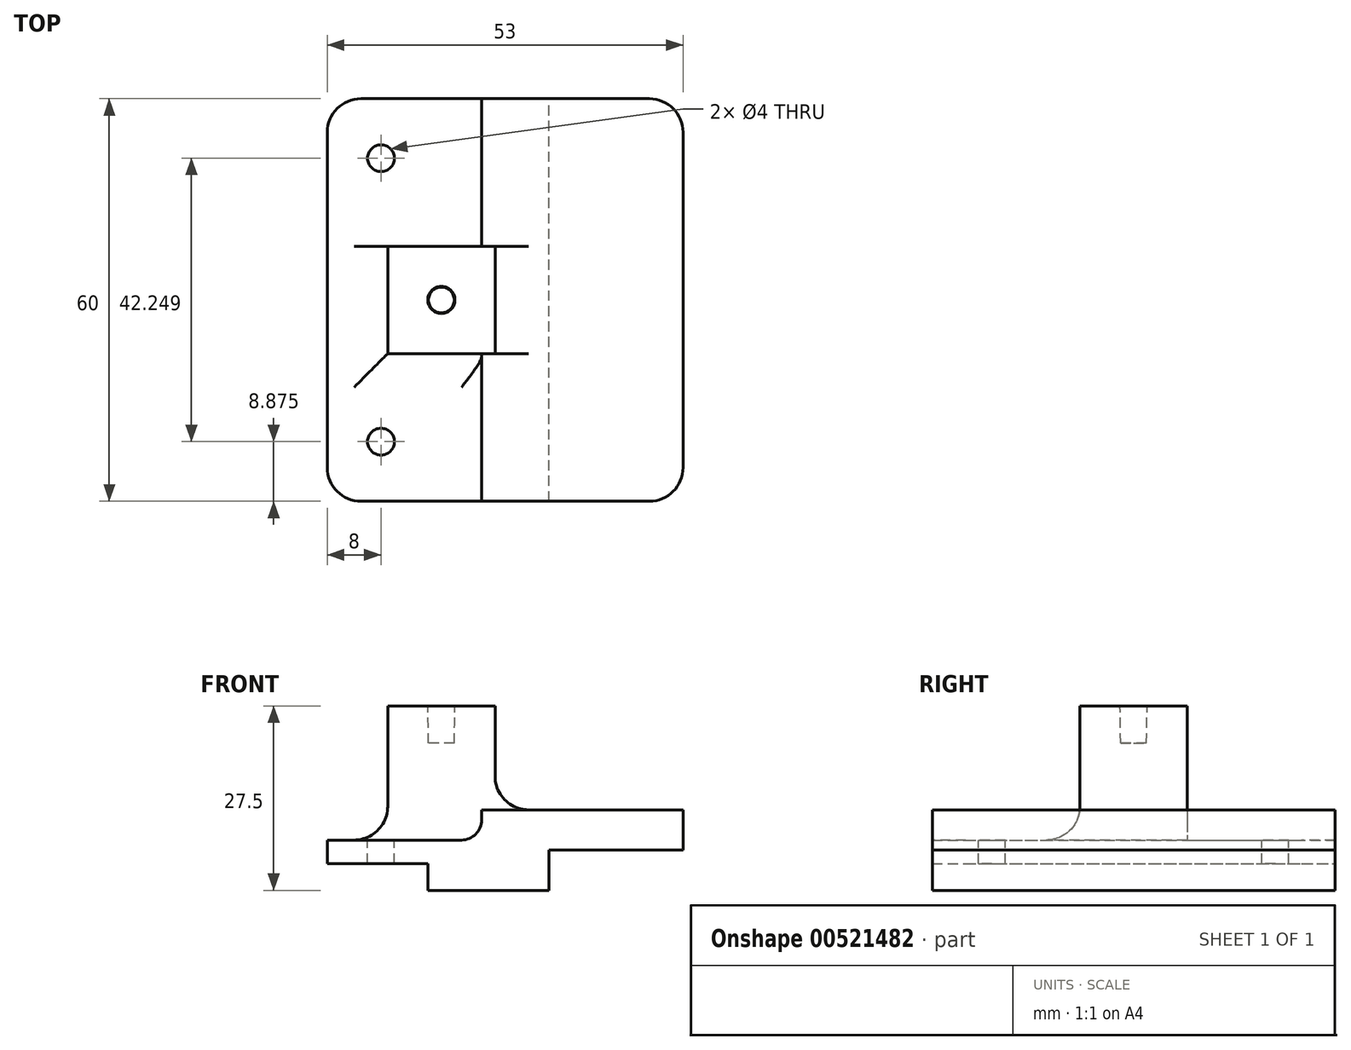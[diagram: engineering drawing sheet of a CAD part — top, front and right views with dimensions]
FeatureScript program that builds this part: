
annotation { "Feature Type Name" : "Feature", "Feature Type Description" : "" }
export const myFeature = defineFeature(function(context is Context, id is Id, definition is map)
    precondition{}
    {
        {
            var Q0;
            Q0=qCreatedBy(makeId("Front.planeOp"),FACE);
            var sketch = newSketch(context, id + "F0", { "sketchPlane" : qUnion([Q0])});
            skLineSegment(sketch, "E0", {"start": v(-15, 0) * mm, "end": v(-15, 3.5) * mm});
            skLineSegment(sketch, "E1", {"start": v(-15, 3.5) * mm, "end": v(8, 3.5) * mm});
            skLineSegment(sketch, "E2", {"start": v(8, 3.5) * mm, "end": v(8, 8) * mm});
            skLineSegment(sketch, "E3", {"start": v(8, 8) * mm, "end": v(38, 8) * mm});
            skLineSegment(sketch, "E4", {"start": v(38, 8) * mm, "end": v(38, 2) * mm});
            skLineSegment(sketch, "E5", {"start": v(38, 2) * mm, "end": v(18, 2) * mm});
            skLineSegment(sketch, "E6", {"start": v(18, 2) * mm, "end": v(18, -4) * mm});
            skLineSegment(sketch, "E7", {"start": v(18, -4) * mm, "end": v(0, -4) * mm});
            skLineSegment(sketch, "E8", {"start": v(0, -4) * mm, "end": v(0, 0) * mm});
            skLineSegment(sketch, "E9", {"start": v(0, 0) * mm, "end": v(-15, 0) * mm});
            skSolve(sketch);
        }
        {
            var Q0;
            Q0=makeQuery(id+"F0.imprint","IMPRINT",FACE,{"disambiguationData":[TD([[makeQuery(id+"F0.imprint","IMPRINT",EDGE,{"derivedFrom":sQuery(id+"F0.wireOp",EDGE,"E0")}),-1.0]])]});
            extrude(context, id + "F1", {"entities" : qUnion([Q0]), "endBound" : BoundingType.SYMMETRIC, "depth" : 60 * mm, "offsetDistance" : 25 * mm});
        }
        {
            var Q0;
            Q0=makeQuery(id+"F1.opExtrude","SWEPT_FACE",FACE,{"disambiguationData":[OSD([sQuery(id+"F0.wireOp",EDGE,"E1")])]});
            var sketch = newSketch(context, id + "F2", { "sketchPlane" : qUnion([Q0])});
            skLineSegment(sketch, "E10", {"start": v(-7, 21.12) * mm, "end": v(-7, -21.12) * mm, "construction": true});
            skCircle(sketch, "E11", {"center": v(-7, 21.12) * mm, "radius": 2 * mm});
            skCircle(sketch, "E12", {"center": v(-7, -21.12) * mm, "radius": 2 * mm});
            skPoint(sketch, "E13", {"position": v(-7, 0) * mm});
            skLineSegment(sketch, "E14.bottom", {"start": v(-15, 8) * mm, "end": v(1, 8) * mm});
            skLineSegment(sketch, "E14.top", {"start": v(-15, -8) * mm, "end": v(1, -8) * mm});
            skLineSegment(sketch, "E14.left", {"start": v(-15, 8) * mm, "end": v(-15, -8) * mm});
            skLineSegment(sketch, "E14.right", {"start": v(1, 8) * mm, "end": v(1, -8) * mm});
            skSolve(sketch);
        }
        {
            var Q0;
            Q0=makeQuery(id+"F2.imprint","IMPRINT",FACE,{"disambiguationData":[TD([[makeQuery(id+"F2.imprint","IMPRINT",EDGE,{"derivedFrom":sQuery(id+"F2.wireOp",EDGE,"E14.bottom")}),-1.0]])]});
            extrude(context, id + "F3", {"entities" : qUnion([Q0]), "operationType" : NewBodyOperationType.ADD, "depth" : 20 * mm, "offsetDistance" : 25 * mm});
        }
        {
            var Q0;
            Q0=makeQuery(id+"F2.imprint","IMPRINT",FACE,{"disambiguationData":[TD([[makeQuery(id+"F2.imprint","IMPRINT",EDGE,{"derivedFrom":sQuery(id+"F2.wireOp",EDGE,"E11")}),1.0]])]});
            var Q1;
            Q1=makeQuery(id+"F2.imprint","IMPRINT",FACE,{"disambiguationData":[TD([[makeQuery(id+"F2.imprint","IMPRINT",EDGE,{"derivedFrom":sQuery(id+"F2.wireOp",EDGE,"E12")}),1.0]])]});
            extrude(context, id + "F4", {"entities" : qUnion([Q0, Q1]), "operationType" : NewBodyOperationType.REMOVE, "oppositeDirection" : true, "depth" : 25 * mm, "offsetDistance" : 25 * mm});
        }
        {
            var Q0;
            Q0=makeQuery(id+"F3.opExtrude","SWEPT_FACE",FACE,{"disambiguationData":[OSD([sQuery(id+"F2.wireOp",EDGE,"E14.right")])]});
            extrude(context, id + "F5", {"entities" : qUnion([Q0]), "operationType" : NewBodyOperationType.ADD, "depth" : 9 * mm, "offsetDistance" : 25 * mm});
        }
        {
            var Q0;
            Q0=makeQuery(id+"F3.boolean.opBoolean","MERGE",FACE,{"derivedFrom":[makeQuery(id+"F1.opExtrude","SWEPT_FACE",FACE,{"disambiguationData":[OSD([sQuery(id+"F0.wireOp",EDGE,"E0")])]}),makeQuery(id+"F3.opExtrude","SWEPT_FACE",FACE,{"disambiguationData":[OSD([sQuery(id+"F2.wireOp",EDGE,"E14.left")])]})]});
            var sketch = newSketch(context, id + "F6", { "sketchPlane" : qUnion([Q0])});
            skLineSegment(sketch, "E15.bottom", {"start": v(-8, 23.5) * mm, "end": v(8, 23.5) * mm});
            skLineSegment(sketch, "E15.top", {"start": v(-8, 3.5) * mm, "end": v(8, 3.5) * mm});
            skLineSegment(sketch, "E15.left", {"start": v(-8, 23.5) * mm, "end": v(-8, 3.5) * mm});
            skLineSegment(sketch, "E15.right", {"start": v(8, 23.5) * mm, "end": v(8, 3.5) * mm});
            skSolve(sketch);
        }
        {
            var Q0;
            Q0=makeQuery(id+"F6.imprint","IMPRINT",FACE,{"disambiguationData":[TD([[makeQuery(id+"F6.imprint","IMPRINT",EDGE,{"derivedFrom":sQuery(id+"F6.wireOp",EDGE,"E15.bottom")}),1.0]])]});
            extrude(context, id + "F7", {"entities" : qUnion([Q0]), "operationType" : NewBodyOperationType.REMOVE, "oppositeDirection" : true, "depth" : 9 * mm, "offsetDistance" : 25 * mm});
        }
        {
            var Q0;
            Q0=makeQuery(id+"F1.opExtrude","SWEPT_EDGE",EDGE,{"disambiguationData":[OSD([sQuery(id+"F0.wireOp",EDGE,"E1"),sQuery(id+"F0.wireOp",EDGE,"E2")])]});
            fillet(context, id + "F8", {"entities" : qUnion([Q0]), "radius" : 3 * mm, "tangentPropagation" : true, "allowEdgeOverflow" : false});
        }
        {
            var Q0;
            Q0=makeQuery(id+"F1.opExtrude","CAP_EDGE",EDGE,{"disambiguationData":[OSD([sQuery(id+"F0.wireOp",EDGE,"E0")])],"isStart":false});
            var Q1;
            Q1=makeQuery(id+"F1.opExtrude","CAP_EDGE",EDGE,{"disambiguationData":[OSD([sQuery(id+"F0.wireOp",EDGE,"E0")])],"isStart":true});
            var Q2;
            Q2=makeQuery(id+"F1.opExtrude","CAP_EDGE",EDGE,{"disambiguationData":[OSD([sQuery(id+"F0.wireOp",EDGE,"E4")])],"isStart":false});
            var Q3;
            Q3=makeQuery(id+"F1.opExtrude","CAP_EDGE",EDGE,{"disambiguationData":[OSD([sQuery(id+"F0.wireOp",EDGE,"E4")])],"isStart":true});
            fillet(context, id + "F9", {"entities" : qUnion([Q0, Q1, Q2, Q3]), "radius" : 5 * mm, "tangentPropagation" : true, "allowEdgeOverflow" : false});
        }
        {
            var Q0;
            Q0=makeQuery(id+"F7.boolean.opBoolean","COPY",EDGE,{"derivedFrom":makeQuery(id+"F7.opExtrude","CAP_EDGE",EDGE,{"disambiguationData":[OSD([sQuery(id+"F6.wireOp",EDGE,"E15.top")])],"isStart":false})});
            var Q1;
            {var subQ0=sQuery(id+"F2.wireOp",EDGE,"E14.right");var subQ1=sQuery(id+"F2.wireOp",EDGE,"E14.top");Q1=makeQuery(id+"F5.boolean.opBoolean","MERGE",EDGE,{"derivedFrom":[makeQuery(id+"F3.opExtrude","CAP_EDGE",EDGE,{"disambiguationData":[OSD([subQ1])],"isStart":true}),makeQuery(id+"F5.opExtrude","SWEPT_EDGE",EDGE,{"disambiguationData":[OSD([subQ1,subQ0]),TDD([makeQuery(id+"F3.opExtrude","CAP_VERTEX",VERTEX,{"disambiguationData":[OSD([subQ1,subQ0])],"isStart":true})])]})]});}
            var Q2;
            {var subQ0=sQuery(id+"F2.wireOp",EDGE,"E14.right");var subQ1=sQuery(id+"F2.wireOp",EDGE,"E14.bottom");Q2=makeQuery(id+"F5.boolean.opBoolean","MERGE",EDGE,{"derivedFrom":[makeQuery(id+"F3.opExtrude","CAP_EDGE",EDGE,{"disambiguationData":[OSD([subQ1])],"isStart":true}),makeQuery(id+"F5.opExtrude","SWEPT_EDGE",EDGE,{"disambiguationData":[OSD([subQ1,subQ0]),TDD([makeQuery(id+"F3.opExtrude","CAP_VERTEX",VERTEX,{"disambiguationData":[OSD([subQ1,subQ0])],"isStart":true})])]})]});}
            fillet(context, id + "F10", {"entities" : qUnion([Q0, Q1, Q2]), "radius" : 5 * mm, "tangentPropagation" : true, "allowEdgeOverflow" : false});
        }
        {
            var Q0;
            Q0=makeQuery(id+"F3.opExtrude","CAP_FACE",FACE,{"disambiguationData":[OSD([sQuery(id+"F2.wireOp",EDGE,"E14.bottom"),sQuery(id+"F2.wireOp",EDGE,"E14.top"),sQuery(id+"F2.wireOp",EDGE,"E14.left"),sQuery(id+"F2.wireOp",EDGE,"E14.right")])],"isStart":false});
            var sketch = newSketch(context, id + "F11", { "sketchPlane" : qUnion([Q0])});
            skCircle(sketch, "E16", {"center": v(2, 0) * mm, "radius": 2.02 * mm});
            skLineSegment(sketch, "E17", {"start": v(2, 8) * mm, "end": v(2, 0) * mm, "construction": true});
            skSolve(sketch);
        }
        {
            var Q0;
            Q0=makeQuery(id+"F11.imprint","IMPRINT",FACE,{"disambiguationData":[TD([[makeQuery(id+"F11.imprint","IMPRINT",EDGE,{"derivedFrom":sQuery(id+"F11.wireOp",EDGE,"E16")}),1.0]])]});
            extrude(context, id + "F12", {"entities" : qUnion([Q0]), "operationType" : NewBodyOperationType.REMOVE, "oppositeDirection" : true, "depth" : 5.56 * mm, "offsetDistance" : 25 * mm, "hasDraft" : true, "draftAngle" : 1 * degree, "draftPullDirection" : true});
        }
        {
            var Q0;
            Q0=makeQuery(id+"F5.boolean.opBoolean","INTERSECT",EDGE,{"derivedFrom":[makeQuery(id+"F1.opExtrude","SWEPT_FACE",FACE,{"disambiguationData":[OSD([sQuery(id+"F0.wireOp",EDGE,"E3")])]}),makeQuery(id+"F5.opExtrude","CAP_FACE",FACE,{"disambiguationData":[OSD([sQuery(id+"F2.wireOp",EDGE,"E14.right")])],"isStart":false})]});
            fillet(context, id + "F13", {"entities" : qUnion([Q0]), "radius" : 5 * mm, "tangentPropagation" : true, "allowEdgeOverflow" : false});
        }
    });
